# Revit family: FU_Chair_Sandler_Stak 1-1
name_source: partatom
category: Furniture
units: mm (PartAtom-declared; Revit-internal decimal feet)

## family parameters
Always vertical = Yes
Cut with Voids When Loaded = No
OmniClass Number = 23.40.20.00
OmniClass Title = General Furniture and Specialties
Room Calculation Point = No
Shared = No
Work Plane-Based = No

## types (1)
- Stak 1.1
    Default Elevation = 0 mm  [stored 0 ft]
    Depth = 495 mm  [stored 1.62402 ft]
    Description = Stacking chair with pressed mild steel seat and back on a tubular steel frame. Zinc-treated for outdoor use and finished with UV-resistant powdercoat. MOQ of 20pcs for painted frames with custom colours. MOQ of 50pcs for chrome frames with custom colours.
    Height = 750 mm  [stored 2.46063 ft]
    Manufacturer = Sandler
    Model = Stak 1.1
    URL = https://www.sandlerseating.com
    Width = 555 mm  [stored 1.82087 ft]

note: [stored X ft] marks values corroborated as IEEE doubles in the binary element streams (Revit-internal decimal feet)

## geometry (parser evidence)
native form markers: Sweep x5
no freeform markers — native parametric forms only
